# Revit family: r2018_videomax_storage
name_source: partatom
category: Устройства связи
revit_build: Autodesk Revit 2018 (Build: 20181011_1500(x64)
units: mm (PartAtom-declared; Revit-internal decimal feet)

## family parameters
Общий = Нет
Основа = Грань
При загрузке вырезать с полостями = Нет
Размер круглого соединителя = Использовать диаметр
Сохранять ориентацию аннотаций = Да
Тип детали = Нормальный
Точка расчета площади = Нет

## types (3) — shared parameters
ADSK_Версия Revit = 2108
ADSK_Версия семейства = v2
ADSK_Единица измерения = шт.
ADSK_Завод-изготовитель = ООО «Видеомакс»
ADSK_Код изделия = ТУ 26.20.21-001-37165186-2020
ADSK_Количество = 1
ADSK_Коэффициент мощности = 0.96
ADSK_Марка = VIDEOMAX-STORAGE
ADSK_Напряжение = 230 В
ADSK_Номинальная мощность = 0 В·А
ADSK_Ток = 0 А
Material = Черный
URL = https://www.videomax-server.ru
Глубина = 560 мм
Изготовитель = ООО «Видеомакс»
Количество входов 230V, шт = 2
Количество интерфейсов Gigabit LAN, шт = 2
Минимальная глубина шкафа, мм = 1000
Тип линейки = PRO
Указания по монтажу = Для монтажа использовать комплектные 19” салазки с параметрами: расстояние между профилями 646 - 940 мм, габариты в сложенном состоянии 757 мм.
Ширина = 430 мм
zero-valued in all types: ADSK_Масса, Количество IP-камер, шт, Количество интерфейсов 10 Gigabit LAN, шт, Максимальная мощность БП, Вт, Максимальная потребляемая мощность Вт, Максимальное тепловыделение, BTU/h, Стоимость

## per-type parameters (varying)
| type | 19” 2U (2ETS) | 19” 3U (3ETS) | 19” 4U (4ETS) | ADSK_Наименование | Back | Front | Высота | Высота в U | Изображение типоразмера | Отметка по умолчанию |
| 19” 2U (2ETS) | Да | Нет | Нет | Сетевое хранилище видеоданных 19” 2U | videomax_19 2U (JBOD) : Back | videomax_19 2U (JBOD) : Front | 88 мм | 2 | 19 (2U) Short.png | 0 мм |
| 19” 3U (3ETS) | Нет | Да | Нет | Сетевое хранилище видеоданных 19” 3U | videomax_19 3U (JBOD) : Back | videomax_19 3U (JBOD) : Front | 131 мм | 3 | 19 (3U) Short.png | 2600 мм |
| 19” 4U (4ETS) | Нет | Нет | Да | Сетевое хранилище видеоданных 19” 4U | videomax_19 4U (JBOD) : Back | videomax_19 4U (JBOD) : Front | 176 мм | 4 | 19 (4U) Short.png | 2600 мм |

note: column(s) folded — value = type name in every type: ADSK_Обозначение
